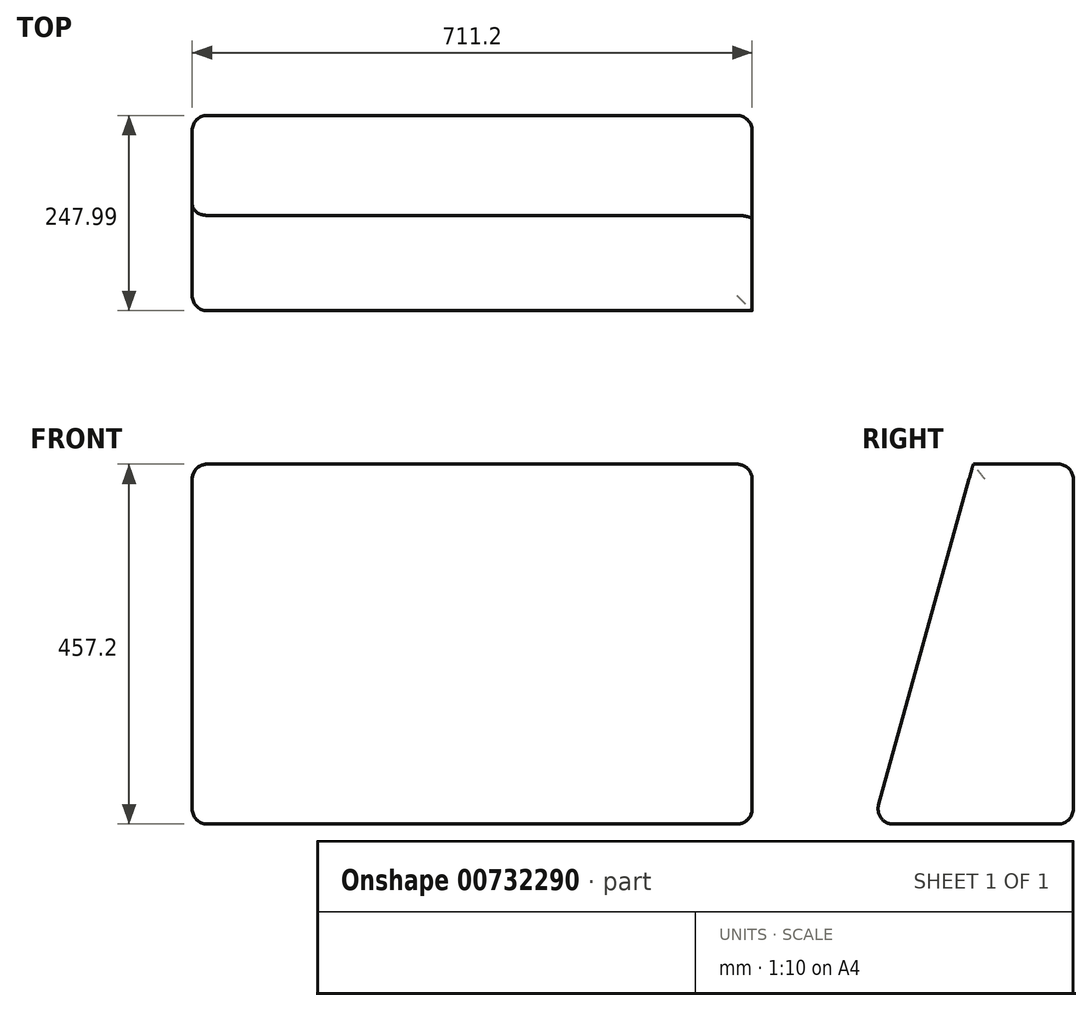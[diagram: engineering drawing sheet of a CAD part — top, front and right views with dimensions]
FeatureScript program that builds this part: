
annotation { "Feature Type Name" : "Feature", "Feature Type Description" : "" }
export const myFeature = defineFeature(function(context is Context, id is Id, definition is map)
    precondition{}
    {
        {
            var Q0;
            Q0=qCreatedBy(makeId("Top.planeOp"),FACE);
            var sketch = newSketch(context, id + "F0", { "sketchPlane" : qUnion([Q0])});
            skLineSegment(sketch, "E0.bottom", {"start": v(355.6, 127) * mm, "end": v(-355.6, 127) * mm});
            skLineSegment(sketch, "E0.top", {"start": v(355.6, -127) * mm, "end": v(-355.6, -127) * mm});
            skLineSegment(sketch, "E0.left", {"start": v(355.6, 127) * mm, "end": v(355.6, -127) * mm});
            skLineSegment(sketch, "E0.right", {"start": v(-355.6, 127) * mm, "end": v(-355.6, -127) * mm});
            skPoint(sketch, "E0.middle", {"position": v(0, 0) * mm});
            skSolve(sketch);
        }
        {
            var Q0;
            Q0 = qSketchRegion(id + "F0", true);
            extrude(context, id + "F1", {"entities" : qUnion([Q0]), "depth" : 457.2 * mm, "offsetDistance" : 25.4 * mm});
        }
        {
            var Q0;
            Q0=makeQuery(id+"F1.opExtrude","SWEPT_FACE",FACE,{"disambiguationData":[OSD([sQuery(id+"F0.wireOp",EDGE,"E0.left")])]});
            var sketch = newSketch(context, id + "F2", { "sketchPlane" : qUnion([Q0])});
            skLineSegment(sketch, "E1", {"start": v(-127, 0) * mm, "end": v(0, 457.2) * mm});
            skSolve(sketch);
        }
        {
            var Q0;
            Q0 = qSketchRegion(id + "F2", true);
            var Q1;
            {var subQ0=sQuery(id+"F2.wireOp",EDGE,"E1");Q1=makeQuery(id+"F2.imprint","IMPRINT",FACE,{"disambiguationData":[TD([[makeQuery(id+"F2.imprint","IMPRINT",EDGE,{"derivedFrom":subQ0}),1.0]])]});}
            extrude(context, id + "F3", {"entities" : qUnion([Q0, Q1]), "operationType" : NewBodyOperationType.REMOVE, "endBound" : BoundingType.THROUGH_ALL, "oppositeDirection" : true, "depth" : 25.4 * mm, "offsetDistance" : 25.4 * mm});
        }
        {
            var Q0;
            {var subQ0=sQuery(id+"F0.wireOp",EDGE,"E0.top");Q0=makeQuery(id+"F3.boolean.opBoolean","MERGE",EDGE,{"derivedFrom":[makeQuery(id+"F1.opExtrude","CAP_EDGE",EDGE,{"disambiguationData":[OSD([subQ0])],"isStart":true}),makeQuery(id+"F3.opExtrude","SWEPT_EDGE",EDGE,{"disambiguationData":[OSD([subQ0,sQuery(id+"F0.wireOp",EDGE,"E0.left"),sQuery(id+"F2.wireOp",EDGE,"E1")])]})]});}
            var Q1;
            Q1=makeQuery(id+"F1.opExtrude","CAP_EDGE",EDGE,{"disambiguationData":[OSD([sQuery(id+"F0.wireOp",EDGE,"E0.left")])],"isStart":true});
            var Q2;
            Q2=makeQuery(id+"F3.boolean.opBoolean","COPY",EDGE,{"derivedFrom":makeQuery(id+"F3.opExtrude","CAP_EDGE",EDGE,{"disambiguationData":[OSD([sQuery(id+"F2.wireOp",EDGE,"E1")])],"isStart":true})});
            var Q3;
            Q3=makeQuery(id+"F3.boolean.opBoolean","INTERSECT",EDGE,{"derivedFrom":[makeQuery(id+"F1.opExtrude","SWEPT_FACE",FACE,{"disambiguationData":[OSD([sQuery(id+"F0.wireOp",EDGE,"E0.right")])]}),makeQuery(id+"F3.opExtrude","SWEPT_FACE",FACE,{"disambiguationData":[OSD([sQuery(id+"F2.wireOp",EDGE,"E1")])]})]});
            var Q4;
            Q4=makeQuery(id+"F1.opExtrude","CAP_EDGE",EDGE,{"disambiguationData":[OSD([sQuery(id+"F0.wireOp",EDGE,"E0.right")])],"isStart":true});
            var Q5;
            Q5=makeQuery(id+"F1.opExtrude","CAP_EDGE",EDGE,{"disambiguationData":[OSD([sQuery(id+"F0.wireOp",EDGE,"E0.right")])],"isStart":false});
            var Q6;
            Q6=makeQuery(id+"F3.boolean.opBoolean","COPY",EDGE,{"derivedFrom":makeQuery(id+"F3.opExtrude","SWEPT_EDGE",EDGE,{"disambiguationData":[OSD([sQuery(id+"F0.wireOp",EDGE,"E0.left"),sQuery(id+"F2.wireOp",EDGE,"E1")])]})});
            var Q7;
            Q7=makeQuery(id+"F1.opExtrude","CAP_EDGE",EDGE,{"disambiguationData":[OSD([sQuery(id+"F0.wireOp",EDGE,"E0.left")])],"isStart":false});
            var Q8;
            Q8=makeQuery(id+"F1.opExtrude","SWEPT_EDGE",EDGE,{"disambiguationData":[OSD([sQuery(id+"F0.wireOp",EDGE,"E0.bottom"),sQuery(id+"F0.wireOp",EDGE,"E0.left")])]});
            var Q9;
            Q9=makeQuery(id+"F1.opExtrude","CAP_EDGE",EDGE,{"disambiguationData":[OSD([sQuery(id+"F0.wireOp",EDGE,"E0.bottom")])],"isStart":true});
            var Q10;
            Q10=makeQuery(id+"F1.opExtrude","SWEPT_EDGE",EDGE,{"disambiguationData":[OSD([sQuery(id+"F0.wireOp",EDGE,"E0.bottom"),sQuery(id+"F0.wireOp",EDGE,"E0.right")])]});
            var Q11;
            Q11=makeQuery(id+"F1.opExtrude","CAP_EDGE",EDGE,{"disambiguationData":[OSD([sQuery(id+"F0.wireOp",EDGE,"E0.bottom")])],"isStart":false});
            fillet(context, id + "F4", {"entities" : qUnion([Q0, Q1, Q2, Q3, Q4, Q5, Q6, Q7, Q8, Q9, Q10, Q11]), "radius" : 19.05 * mm, "tangentPropagation" : true, "allowEdgeOverflow" : false});
        }
    });
